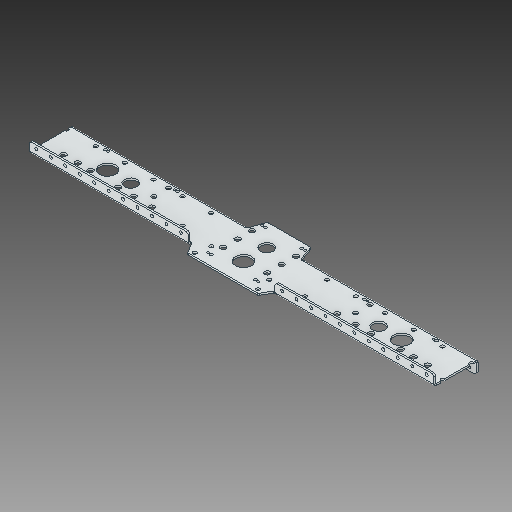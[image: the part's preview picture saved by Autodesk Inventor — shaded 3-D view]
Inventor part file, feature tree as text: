
AUTODESK INVENTOR PART (.ipt)
format: ipt  version: 2018 (Build 220112000, 112)  size: 284,160 bytes
history: native  units: in
note: dims shown in document units (in); Inventor stores cm internally (conversion verified against a paired STEP export)
features: chamfer x1
ambient origin geometry x8: Origin, YZ Plane, XZ Plane, XY Plane, X Axis, Y Axis, Z Axis, Center Point
bodies: Solid1 (feature_tree)
feature tree (1):
  chamfer  "Chamfer2"  [1 undecoded]
note: 1 required parameter value undecoded (feature->parameter linkage not recoverable at this tier; creation-order binding heuristic only, values carry confidence <= 0.55)
